# Revit family: Pump_Rheem_DeliverySkid
name_source: partatom
category: Mechanical Equipment
revit_build: Autodesk Revit 2014 (Build: 20140709_2115(x64)
units: mm (PartAtom-declared; Revit-internal decimal feet)

## types (1)
- This Family Using Type Catalogue
    ActivePower = 0 W
    ApparentPower = 0 W
    BodyMaterial = <By Category>
    ExpectedServiceLifeYears = 0
    FluidDensity = 0.0000 kg/m³
    FluidTemperatureMax = 0 °C
    FluidTemperatureMin = 0 °C
    FluidType = Water
    FullLoadAmps = 0 A
    InletDiameter = 60 mm  [stored 0.19685 ft]
    Manufacturer = Rheem Solahart
    Material = <By Category>
    Model = 0
    MotorAmpsActual = 0 A
    MotorMaterial = <By Category>
    MotorPoles = 0
    MotorSize = 0 W
    MountingType = Floor Mounted
    NCC_SEC_J_Compliance = Yes
    OperatingMass = 0.00 kg
    OperatingTempMax = 0 °C
    OperatingTempMin = 0 °C
    OutletDiameter = 60 mm  [stored 0.19685 ft]
    PipingMaterial = <By Category>
    PowerFactor = 1
    PowerSource = AC
    RunLoadAmps = 0 A
    ShippingMass = 0.00 kg
    SupplyDiameter = 50 mm  [stored 0.164042 ft]
    SupplyFrequency = 50/60 Hz
    SupplyPhase = 1
    SupplyVoltage = 240 V
    TotalHeight = 1368 mm  [stored 4.48819 ft]
    TotalLength = 816 mm  [stored 2.67717 ft]
    TotalWidth = 700 mm
    WarrantyDurationMonths = 0
    XDiameter = 32 mm  [stored 0.104987 ft]

note: [stored X ft] marks values corroborated as IEEE doubles in the binary element streams (Revit-internal decimal feet)

## geometry (parser evidence)
native form markers: Sweep x2
no freeform markers — native parametric forms only
